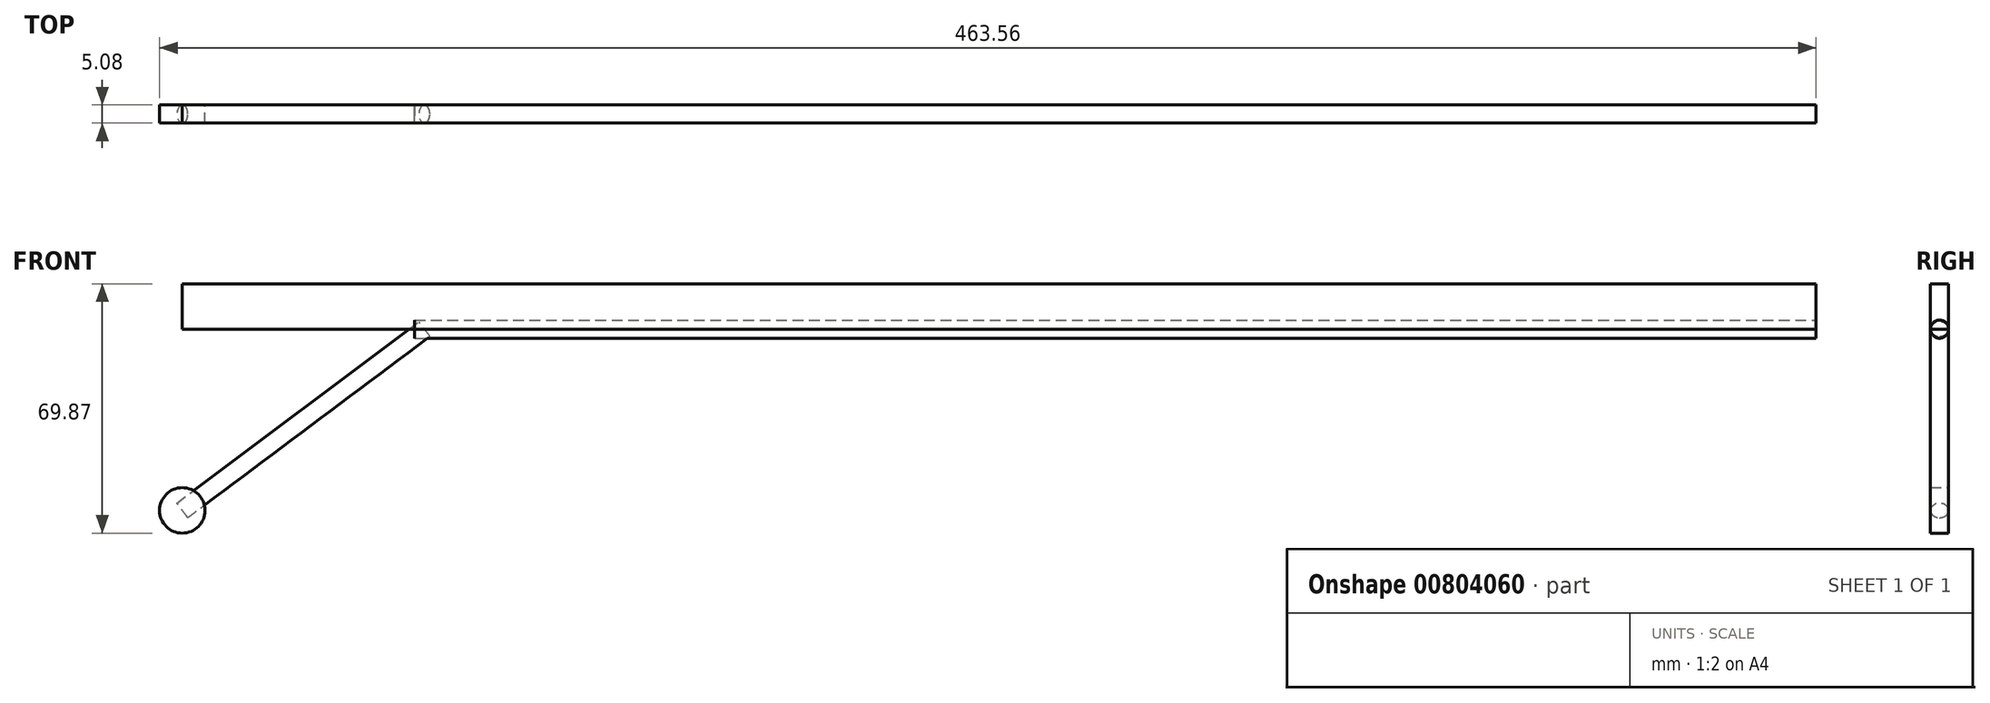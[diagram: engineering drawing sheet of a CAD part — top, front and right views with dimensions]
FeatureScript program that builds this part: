
annotation { "Feature Type Name" : "Feature", "Feature Type Description" : "" }
export const myFeature = defineFeature(function(context is Context, id is Id, definition is map)
    precondition{}
    {
        {
            var Q0;
            Q0=qCreatedBy(makeId("Front.planeOp"),FACE);
            var sketch = newSketch(context, id + "F0", { "sketchPlane" : qUnion([Q0])});
            skLineSegment(sketch, "E0", {"start": v(-188.6, 0) * mm, "end": v(268.6, 0) * mm});
            skLineSegment(sketch, "E1", {"start": v(-188.6, 0) * mm, "end": v(-188.6, -12.7) * mm});
            skLineSegment(sketch, "E2", {"start": v(268.6, 0) * mm, "end": v(268.6, -12.7) * mm});
            skLineSegment(sketch, "E3", {"start": v(-188.6, -12.7) * mm, "end": v(268.6, -12.7) * mm});
            skLineSegment(sketch, "E4", {"start": v(-188.6, -12.7) * mm, "end": v(-188.6, -63.5) * mm, "construction": true});
            skLineSegment(sketch, "E5", {"start": v(-188.6, -12.7) * mm, "end": v(-120.86, -12.7) * mm, "construction": true});
            skCircle(sketch, "E6", {"center": v(-188.6, -63.5) * mm, "radius": 6.37 * mm});
            skSolve(sketch);
        }
        {
            var Q0;
            Q0 = qSketchRegion(id + "F0", true);
            extrude(context, id + "F1", {"entities" : qUnion([Q0]), "endBound" : BoundingType.SYMMETRIC, "depth" : 5.08 * mm, "offsetDistance" : 25.4 * mm});
        }
        {
            var Q0;
            Q0=qCreatedBy(makeId("Front.planeOp"),FACE);
            var sketch = newSketch(context, id + "F2", { "sketchPlane" : qUnion([Q0])});
            skLineSegment(sketch, "E7", {"start": v(-120.86, -12.7) * mm, "end": v(-188.6, -63.5) * mm});
            skLineSegment(sketch, "E8", {"start": v(-188.6, -63.5) * mm, "end": v(-187.07, -65.53) * mm});
            skLineSegment(sketch, "E9", {"start": v(-120.86, -12.7) * mm, "end": v(-119.34, -14.73) * mm});
            skLineSegment(sketch, "E10", {"start": v(-120.86, -12.7) * mm, "end": v(268.6, -12.7) * mm});
            skLineSegment(sketch, "E11", {"start": v(268.6, -12.7) * mm, "end": v(268.6, -15.24) * mm});
            skLineSegment(sketch, "E12", {"start": v(-187.07, -65.53) * mm, "end": v(-119.34, -14.73) * mm});
            skLineSegment(sketch, "E13", {"start": v(-120.86, -12.7) * mm, "end": v(-123.63, -12.7) * mm});
            skLineSegment(sketch, "E14", {"start": v(-123.63, -12.7) * mm, "end": v(-123.63, -15.24) * mm});
            skLineSegment(sketch, "E15", {"start": v(-123.63, -15.24) * mm, "end": v(268.6, -15.24) * mm});
            skSolve(sketch);
        }
        {
            var Q0;
            Q0=makeQuery(id+"F2.imprint","IMPRINT",FACE,{"disambiguationData":[TD([[makeQuery(id+"F2.imprint","IMPRINT",EDGE,{"derivedFrom":sQuery(id+"F2.wireOp",EDGE,"E7")}),1.0]])]});
            var Q1;
            Q1=sQuery(id+"F2.wireOp",EDGE,"E7");
            revolve(context, id + "F3", {"surfaceOperationType" : NewSurfaceOperationType.NEW, "entities" : qUnion([Q0]), "axis" : qUnion([Q1]), "revolveType" : RevolveType.FULL});
        }
        {
            var Q0;
            {var subQ1=sQuery(id+"F2.wireOp",EDGE,"E9");Q0=makeQuery(id+"F2.imprint","IMPRINT",FACE,{"disambiguationData":[TD([[makeQuery(id+"F2.imprint","IMPRINT",EDGE,{"derivedFrom":subQ1}),1.0]])]});}
            var Q1;
            {var subQ0=sQuery(id+"F2.wireOp",EDGE,"E13");Q1=makeQuery(id+"F2.imprint","IMPRINT",FACE,{"disambiguationData":[TD([[makeQuery(id+"F2.imprint","IMPRINT",EDGE,{"derivedFrom":subQ0}),1.0]])]});}
            var Q2;
            {var subQ1=sQuery(id+"F2.wireOp",EDGE,"E9");Q2=makeQuery(id+"F2.imprint","IMPRINT",FACE,{"disambiguationData":[TD([[makeQuery(id+"F2.imprint","IMPRINT",EDGE,{"derivedFrom":subQ1}),-1.0]])]});}
            var Q3;
            Q3=sQuery(id+"F2.wireOp",EDGE,"E13");
            revolve(context, id + "F4", {"surfaceOperationType" : NewSurfaceOperationType.NEW, "entities" : qUnion([Q0, Q1, Q2]), "axis" : qUnion([Q3]), "revolveType" : RevolveType.FULL});
        }
    });
